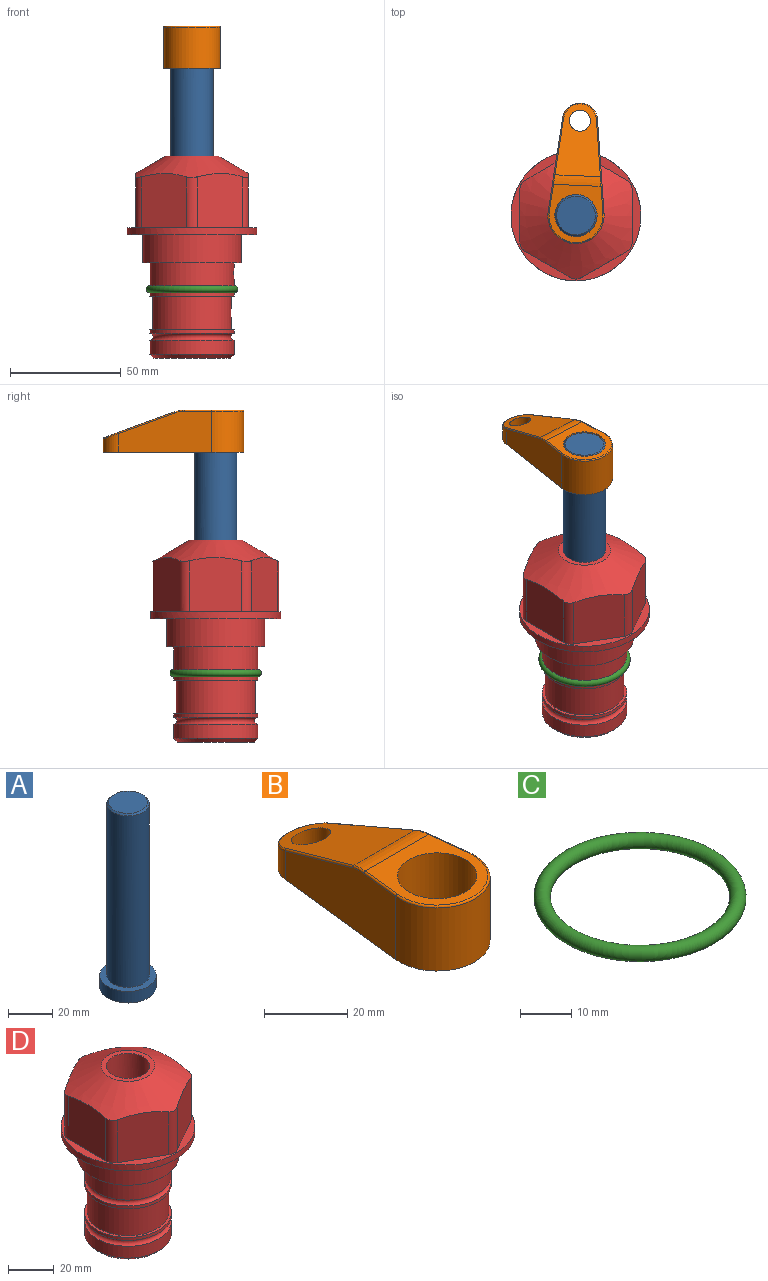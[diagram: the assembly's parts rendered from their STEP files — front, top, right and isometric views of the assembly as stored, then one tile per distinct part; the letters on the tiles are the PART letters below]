
ASSEMBLY  parts=4 mates=2
PART A: 6 faces, bbox 25.4x25.4x101.6 mm
  f0: plane 17.46x17.46mm, normal (0,0,1), area 239.5mm2, adj f5
  f1: plane 25.4x25.4mm, normal (0,0,-1), area 506.7mm2, adj f2
  f2: cylinder r=12.7mm len=25.4mm, axis (0,0,1), area 506.7mm2, adj f1,f3
  f3: plane 25.4x25.4mm, normal (0,0,1), area 221.7mm2, adj f2,f4
  f4: cylinder r=9.53mm len=94.46mm, axis (0,0,1), area 5653mm2, adj f3,f5
  f5: cone r=8.73mm half-angle=45deg, axis (0,0,-1), area 64.4mm2, adj f0,f4
PART B: 44 faces, bbox 27.5x64.5x19.1 mm
  f0: plane 2.3x0.95mm, normal (0,0,-1), area 1mm2, adj f25,f30,f34
  f1: plane 63.5x25.4mm, normal (0,0,-1), area 561.7mm2, adj f2,f3,f4,f5,f6,f7,f19,f20
  f2: cylinder r=12.7mm len=25.4mm, axis (0,0,-1), area 792.2mm2, adj f1,f3,f5,f13
  f3: plane 42.33x18.54mm, normal (0.99,0.11,0), area 647mm2, adj f1,f2,f4,f11,f12,f14
  f4: cylinder r=7.94mm len=15.78mm, axis (0,0,-1), area 158.6mm2, adj f1,f3,f5,f16
  f5: plane 42.33x18.54mm, normal (-0.99,0.11,0), area 647mm2, adj f1,f2,f4,f15,f17,f18
  f6: cylinder r=9.53mm len=19.05mm, axis (0,0,-1), area 1140.1mm2, adj f1,f8
  f7: cylinder r=4.76mm len=10.98mm, axis (0,0,-1), area 276.1mm2, adj f1,f9
  f8: plane 25.83x24.38mm, normal (0,0,1), area 262.2mm2, adj f6,f10,f11,f13,f15
  f9: plane 32.49x20.55mm, normal (0,0.34,0.94), area 489.9mm2, adj f7,f10,f14,f16,f18
  f10: cylinder r=12.7mm len=21.49mm, axis (-1,0,0), area 93.2mm2, adj f8,f9,f12,f17
  f11: cylinder r=0.51mm len=12.34mm, axis (0.11,-0.99,0), area 9.9mm2, adj f3,f8,f12,f13
  f12: bspline ~7.62x1.64mm, area 3.5mm2, adj f3,f10,f11,f14
  f13: torus R=12.19mm, axis (0,0,1), area 33.6mm2, adj f2,f8,f11,f15
  f14: cylinder r=0.51mm len=26.01mm, axis (0.1,-0.93,0.34), area 21.6mm2, adj f3,f9,f12,f16
  f15: cylinder r=0.51mm len=12.34mm, axis (0.11,0.99,0), area 9.9mm2, adj f5,f8,f13,f17
  f16: bspline ~15.78x7.05mm, area 15.7mm2, adj f4,f9,f14,f18
  f17: bspline ~7.62x1.64mm, area 3.5mm2, adj f5,f10,f15,f18
  f18: cylinder r=0.51mm len=26.01mm, axis (0.1,0.93,-0.34), area 21.6mm2, adj f5,f9,f16,f17
  f19: plane 21.6x14.29mm, normal (-0.99,-0.11,0), area 242.6mm2, adj f1,f26,f28,f34,f36,f38
  f20: plane 21.6x14.29mm, normal (0.99,-0.11,0), area 242.6mm2, adj f1,f27,f29,f37,f39,f41
  f21: cylinder r=12.7mm len=14.29mm, axis (0,0,-1), area 173.2mm2, adj f1,f26,f27,f30,f31,f33
  f22: cylinder r=7.94mm len=7.63mm, axis (0,0,-1), area 53.8mm2, adj f1,f28,f29,f42
  f23: plane 2.3x0.95mm, normal (0,0,-1), area 1mm2, adj f25,f33,f37
  f24: plane 17.94x12.32mm, normal (0,-0.34,-0.94), area 191.2mm2, adj f25,f38,f41,f42
  f25: cylinder r=9.53mm len=12.93mm, axis (-1,0,0), area 37.5mm2, adj f0,f23,f24,f31,f36,f39
  f26: cylinder r=1.59mm len=14.29mm, axis (0,0,-1), area 49mm2, adj f1,f19,f21,f32
  f27: cylinder r=1.59mm len=14.29mm, axis (0,0,-1), area 49mm2, adj f1,f20,f21,f35
  f28: cylinder r=1.59mm len=7.28mm, axis (0,0,-1), area 22.1mm2, adj f1,f19,f22,f40
  f29: cylinder r=1.59mm len=7.28mm, axis (0,0,-1), area 22.1mm2, adj f1,f20,f22,f43
  f30: torus R=14.29mm, axis (0,0,1), area 5.8mm2, adj f0,f21,f31,f32
  f31: bspline ~11.06x2.73mm, area 20.8mm2, adj f21,f25,f30,f33
  f32: sphere r=1.59mm, area 5.4mm2, adj f26,f30,f34
  f33: torus R=14.29mm, axis (0,0,1), area 5.8mm2, adj f21,f23,f31,f35
  f34: cylinder r=1.59mm len=1.68mm, axis (-0.11,0.99,0), area 2.4mm2, adj f0,f19,f32,f36
  f35: sphere r=1.59mm, area 5.4mm2, adj f27,f33,f37
  f36: bspline ~5.82x2.33mm, area 7.7mm2, adj f19,f25,f34,f38
  f37: cylinder r=1.59mm len=1.68mm, axis (0.11,0.99,0), area 2.4mm2, adj f20,f23,f35,f39
  f38: cylinder r=1.59mm len=18.33mm, axis (0.1,-0.93,0.34), area 46.7mm2, adj f19,f24,f36,f40
  f39: bspline ~5.82x2.33mm, area 7.7mm2, adj f20,f25,f37,f41
  f40: sphere r=1.59mm, area 3.6mm2, adj f28,f38,f42
  f41: cylinder r=1.59mm len=18.33mm, axis (0.1,0.93,-0.34), area 46.7mm2, adj f20,f24,f39,f43
  f42: bspline ~8.31x1.84mm, area 15.3mm2, adj f22,f24,f40,f43
  f43: sphere r=1.59mm, area 3.6mm2, adj f29,f41,f42
PART C: 1 faces, bbox 44.7x44.7x3.2 mm
  f0: torus R=19.05mm, axis (0,0,1), area 1193.9mm2
PART D: 36 faces, bbox 58.7x58.7x91.2 mm
  f0: cylinder r=17.78mm len=35.56mm, axis (0,0,1), area 1670.8mm2, adj f23,f24,f31
  f1: cylinder r=19.05mm len=38.1mm, axis (0,0,1), area 1191.9mm2, adj f26,f27,f30
  f2: plane 58.66x58.66mm, normal (0,0,-1), area 1150.6mm2, adj f3,f28
  f3: cylinder r=29.33mm len=58.66mm, axis (0,0,-1), area 585.1mm2, adj f2,f4
  f4: plane 58.66x58.66mm, normal (0,0,1), area 475.9mm2, adj f3,f5,f6,f7,f8,f9,f10,f11
  f5: plane 24.5x20.32mm, normal (-0.5,0.87,0), area 562.8mm2, adj f4,f15,f16,f17
  f6: plane 24.5x20.32mm, normal (0.5,0.87,0), area 562.8mm2, adj f4,f14,f15,f17
  f7: plane 24.5x23.48mm, normal (1,0,0), area 562.8mm2, adj f4,f13,f14,f17
  f8: plane 24.5x20.32mm, normal (0.5,-0.87,0), area 562.8mm2, adj f4,f12,f13,f17
  f9: plane 24.5x20.32mm, normal (-0.5,-0.87,0), area 562.8mm2, adj f4,f11,f12,f17
  f10: plane 24.5x23.48mm, normal (-1,0,0), area 562.8mm2, adj f4,f11,f16,f17
  f11: cylinder r=5.08mm len=23.01mm, axis (0,0,-1), area 121.2mm2, adj f4,f9,f10,f17
  f12: cylinder r=5.08mm len=23.01mm, axis (0,0,-1), area 121.2mm2, adj f4,f8,f9,f17
  f13: cylinder r=5.08mm len=23.01mm, axis (0,0,-1), area 121.2mm2, adj f4,f7,f8,f17
  f14: cylinder r=5.08mm len=23.01mm, axis (0,0,-1), area 121.2mm2, adj f4,f6,f7,f17
  f15: cylinder r=5.08mm len=23.01mm, axis (0,0,-1), area 121.2mm2, adj f4,f5,f6,f17
  f16: cylinder r=5.08mm len=23.01mm, axis (0,0,-1), area 121.2mm2, adj f4,f5,f10,f17
  f17: cone r=11.73mm half-angle=60deg, axis (0,0,-1), area 2071.8mm2, adj f5,f6,f7,f8,f9,f10,f11,f12
  f18: plane 23.46x23.46mm, normal (0,0,1), area 147.4mm2, adj f17,f35
  f19: plane 34.93x34.93mm, normal (0,0,-1), area 958mm2, adj f29
  f20: cylinder r=19.05mm len=38.1mm, axis (0,0,1), area 760.1mm2, adj f21,f29
  f21: torus R=19.05mm, axis (0,0,1), area 565.3mm2, adj f20,f22
  f22: cylinder r=19.05mm len=38.1mm, axis (0,0,1), area 190mm2, adj f21,f23
  f23: plane 38.1x38.1mm, normal (0,0,1), area 146.9mm2, adj f0,f22
  f24: plane 38.1x38.1mm, normal (0,0,-1), area 146.9mm2, adj f0,f25
  f25: cylinder r=19.05mm len=38.1mm, axis (0,0,1), area 190mm2, adj f24,f26
  f26: torus R=19.05mm, axis (0,0,1), area 565.3mm2, adj f1,f25
  f27: plane 44.45x44.45mm, normal (0,0,-1), area 411.7mm2, adj f1,f28
  f28: cylinder r=22.23mm len=44.45mm, axis (0,0,1), area 1773.5mm2, adj f2,f27
  f29: cone r=19.05mm half-angle=45deg, axis (0,0,1), area 257.5mm2, adj f19,f20
  f30: cylinder r=3.17mm len=6.75mm, axis (-1,0,0), area 128mm2, adj f1,f33
  f31: cylinder r=3.17mm len=6.35mm, axis (-1,0,0), area 102.5mm2, adj f0,f33
  f32: plane 25.4x25.4mm, normal (0,0,1), area 506.7mm2, adj f33
  f33: cylinder r=12.7mm len=66.42mm, axis (0,0,-1), area 5236.2mm2, adj f30,f31,f32,f34
  f34: cone r=9.53mm half-angle=30deg, axis (0,0,-1), area 443.4mm2, adj f33,f35
  f35: cylinder r=9.53mm len=19.05mm, axis (0,0,-1), area 849mm2, adj f18,f34
PLACE A rot(axis=(0,0,-1),2.4deg) t=(0,0,20.59)mm
PLACE B rot(axis=(0,0,-1),2.4deg) t=(0,0,75.2)mm
PLACE C at identity
PLACE D at identity fixed
MATE fastened B.f2 <-> A.f2  axis (0,0,-1) through (0,0,94.25)mm
MATE cylindrical A.f2 <-> D.f0  axis (0,0,1) through (0,0,46.23)mm
